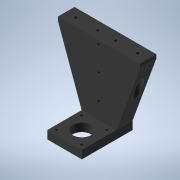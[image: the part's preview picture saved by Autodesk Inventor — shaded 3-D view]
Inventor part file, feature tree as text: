
AUTODESK INVENTOR PART (.ipt)
format: ipt  version: 2021 (Build 250183000, 183)  size: 169,984 bytes
history: native  units: mm
features: extrude x5, sketch x4, projected_geometry x1
ambient origin geometry x8: Origin, YZ Plane, XZ Plane, XY Plane, X Axis, Y Axis, Z Axis, Center Point
bodies: Solid1 (feature_tree)
feature tree (10):
  extrude  "Extrusion1"  Depth=10.0mm
  extrude  "Extrusion2"  Depth=95.0mm
  sketch  "Sketch3"  dims[d4=100.0mm d5=20.0mm d6=0.0mm]
  extrude  "Extrusion3"  Depth=20.0mm TaperAngle=0.0deg
  extrude  "Extrusion5"  Depth=10.0mm
  extrude  "Extrusion4"  Depth=10.0mm
  sketch  "Sketch1"  dims[d0=42.0mm d1=10.0mm]
  sketch  "Sketch2"  dims[d2=5.0mm d3=95.0mm]
  projected_geometry  "Projected Loop1"
  sketch  "Sketch4"  dims[d7=22.5mm d8=31.0mm d9=31.0mm d10=15.5mm d11=15.5mm d12=3.5mm d13=10.0mm d14=0.0mm d15=12.0mm d16=4.3mm d17=10.0mm d18=12.0mm d19=10.0mm d20=10.0mm d21=92.0mm d22=0.0mm d23=5.0mm d24=30.0mm d25=30.0mm d26=4.2mm d27=10.0mm d28=0.0mm d29=0.0mm d30=0.0mm]
